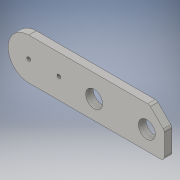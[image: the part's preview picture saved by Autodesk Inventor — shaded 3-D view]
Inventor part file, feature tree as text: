
AUTODESK INVENTOR PART (.ipt)
format: ipt  version: 2016 (Build 200138000, 138)  size: 139,776 bytes
history: native  units: in
note: dims shown in document units (in); Inventor stores cm internally (conversion verified against a paired STEP export)
features: sketch x4, extrude x3, projected_geometry x3
ambient origin geometry x8: Origin, YZ Plane, XZ Plane, XY Plane, X Axis, Y Axis, Z Axis, Center Point
bodies: Body1 (feature_tree)
feature tree (10):
  extrude  "Extrusion10"  Depth=2.75in
  extrude  "Extrusion11"  Depth=1.125in
  sketch  "Sketch9"  dims[d72=0.25in d73=0.5in d74=0.0in]
  extrude  "Extrusion12"  Depth=0.5in TaperAngle=0.0deg
  sketch  "Sketch1"  dims[d61=2.75in d68=8.75in]
  sketch  "Sketch8"  dims[d69=7.8964in d71=1.125in]
  projected_geometry  "Projected Loop3"
  projected_geometry  "Projected Loop4"
  sketch  "Sketch10"  dims[d75=4.0in d76=3.5in d77=1.125in d78=0.25in d79=0.0in d80=2.0in d81=11.2125in d82=2.0in d83=0.25in d84=1.0in d85=0.0in]
  projected_geometry  "Projected Loop5"
